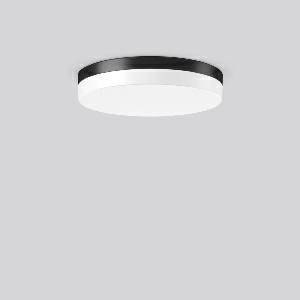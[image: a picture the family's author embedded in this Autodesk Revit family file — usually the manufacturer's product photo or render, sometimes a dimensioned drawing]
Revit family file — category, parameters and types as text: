
# Revit family: flat_slim_round_312676_0031_19_fd8e
name_source: partatom
category: Lighting Fixtures
units: mm (PartAtom-declared; Revit-internal decimal feet)

## family parameters
Cut with Voids When Loaded = No
Host = Face
Light Source = No
Part Type = Normal
Room Calculation Point = No
Round Connector Dimension = Use Diameter
Shared = No

## types (1)
- MultiLumen 1 830 (1 x LED Modul 830, 2400 lm, 3000)
    Apparent Load = 20 VA
    CIE Flux Codes = 39 70 90 83 100
    Color Rendering = 80
    Color Temperature = 3000
    Default Elevation = 1800 mm
    Height = 70 mm
    Lamp = 1 x LED Modul 830
    Lamp Light Flux = 2400 lm
    Lamp count = 1
    Length = 400 mm
    Lifetime = 50000 h
    Luminous efficacy = 120 lm/W
    Manufacturer = RZB
    ModVariant = No
    Model = 312676.0031.19
    Mounting Place = Ceiling
    Mounting Type = Surface mounted
    Number of Poles = 1
    OnlyDefault = Yes
    Power Factor = 1
    Product Name = FLAT SLIM round
    Product group = Surface mounted ceiling and wall luminaires
    ProductGroupID = 305
    Protection Class = Protection class I
    Protection Degree = Degree of protection
    RLX_Detail_Level = 1
    RLX_Emergency_Light_Flux = 0 lm
    RLX_Emergency_Type = 0
    RLX_Emergency_Type_DB = No
    RlxData = <blob elided: 22033 chars, md5=1de61c8c>
    Socket = socket
    Standby Power = 0 W
    System Light Flux = 2400 lm
    System Power = 20 W
    Type Comments = MultiLumen 1 830
    Type Image = 312631.0031.jpg
    URL = http://relux.com
    VarID = multilumen_1_830
    Voltage = 0 V
    Weight = 0.00 kg
    Width = 0 mm  [stored 0 ft]

note: [stored X ft] marks values corroborated as IEEE doubles in the binary element streams (Revit-internal decimal feet)

## geometry (parser evidence)
native form markers: Blend x4, Sweep x12
no freeform markers — native parametric forms only
